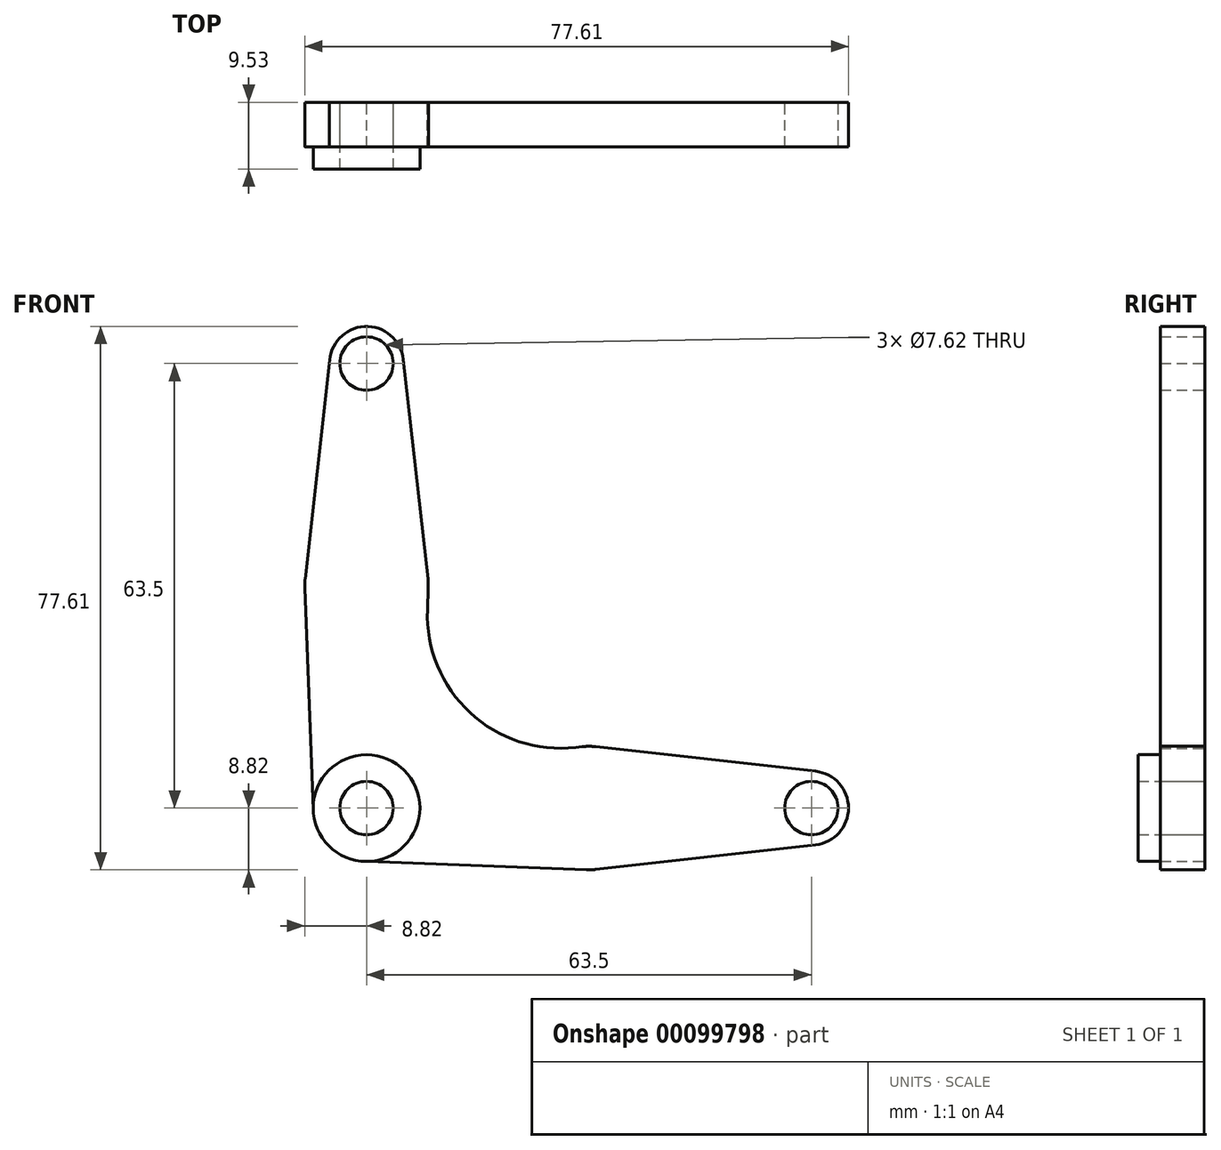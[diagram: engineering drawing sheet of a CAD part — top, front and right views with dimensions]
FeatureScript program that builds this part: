
annotation { "Feature Type Name" : "Feature", "Feature Type Description" : "" }
export const myFeature = defineFeature(function(context is Context, id is Id, definition is map)
    precondition{}
    {
        {
            var Q0;
            Q0=qCreatedBy(makeId("Front.planeOp"),FACE);
            var sketch = newSketch(context, id + "F0", { "sketchPlane" : qUnion([Q0])});
            skLineSegment(sketch, "E0", {"start": v(0, 0) * mm, "end": v(63.5, 0) * mm, "construction": true});
            skCircle(sketch, "E1", {"center": v(0, 63.5) * mm, "radius": 5.3 * mm});
            skCircle(sketch, "E2", {"center": v(0, 31.75) * mm, "radius": 8.82 * mm});
            skCircle(sketch, "E3", {"center": v(0, 0) * mm, "radius": 7.62 * mm});
            skCircle(sketch, "E4", {"center": v(63.5, 0) * mm, "radius": 5.3 * mm});
            skLineSegment(sketch, "E5", {"start": v(-5.3, 63.5) * mm, "end": v(-8.76, 32.74) * mm});
            skLineSegment(sketch, "E6", {"start": v(8.76, 32.73) * mm, "end": v(5.26, 64.09) * mm});
            skLineSegment(sketch, "E7", {"start": v(0, 63.5) * mm, "end": v(0, 0) * mm, "construction": true});
            skCircle(sketch, "E8", {"center": v(0, 63.5) * mm, "radius": 3.81 * mm});
            skCircle(sketch, "E9", {"center": v(0, 0) * mm, "radius": 3.81 * mm});
            skCircle(sketch, "E10", {"center": v(63.5, 0) * mm, "radius": 3.81 * mm});
            skLineSegment(sketch, "E11", {"start": v(-8.81, 31.42) * mm, "end": v(-7.61, -0.29) * mm});
            skLineSegment(sketch, "E12", {"start": v(8.81, 31.42) * mm, "end": v(8.7, 28.31) * mm});
            skCircle(sketch, "E13", {"center": v(31.75, 0) * mm, "radius": 8.82 * mm});
            skLineSegment(sketch, "E14", {"start": v(29.85, 8.66) * mm, "end": v(30.77, 8.76) * mm});
            skLineSegment(sketch, "E15", {"start": v(0, -7.62) * mm, "end": v(31.42, -8.81) * mm});
            skLineSegment(sketch, "E16", {"start": v(32.73, 8.76) * mm, "end": v(64.09, 5.26) * mm});
            skLineSegment(sketch, "E17", {"start": v(32.73, -8.76) * mm, "end": v(64.09, -5.26) * mm});
            skPoint(sketch, "E18.newPointB", {"position": v(0, 5.32) * mm});
            skArc(sketch, "E18.filletArc", {"start": v(8.7, 28.31) * mm, "mid": v(14.77, 13.64) * mm, "end": v(29.85, 8.66) * mm});
            skSolve(sketch);
        }
        {
            var Q0;
            Q0=makeQuery(id+"F0.imprint","IMPRINT",FACE,{"disambiguationData":[TD([[makeQuery(id+"F0.imprint","IMPRINT",EDGE,{"derivedFrom":sQuery(id+"F0.wireOp",EDGE,"yJPejFJz-5Hof-ibUk-N60A-88DD0Kfbzzva")}),1.0]])]});
            var Q1;
            Q1=makeQuery(id+"F0.imprint","IMPRINT",FACE,{"disambiguationData":[TD([[makeQuery(id+"F0.imprint","IMPRINT",EDGE,{"derivedFrom":sQuery(id+"F0.wireOp",EDGE,"yJPejFJz-5Hof-ibUk-N60A-88DD0Kfbzzva")}),-1.0]])]});
            var Q2;
            Q2=makeQuery(id+"F0.imprint","IMPRINT",FACE,{"disambiguationData":[TD([[makeQuery(id+"F0.imprint","IMPRINT",EDGE,{"derivedFrom":sQuery(id+"F0.wireOp",EDGE,"E10")}),-1.0]])]});
            var Q3;
            {var subQ0=sQuery(id+"F0.wireOp",EDGE,"E5");Q3=makeQuery(id+"F0.imprint","IMPRINT",FACE,{"disambiguationData":[TD([[makeQuery(id+"F0.imprint","IMPRINT",EDGE,{"derivedFrom":subQ0}),1.0]])]});}
            var Q4;
            Q4=makeQuery(id+"F0.imprint","IMPRINT",FACE,{"disambiguationData":[TD([[makeQuery(id+"F0.imprint","IMPRINT",EDGE,{"derivedFrom":sQuery(id+"F0.wireOp",EDGE,"E8")}),-1.0]])]});
            var Q5;
            {var subQ1=sQuery(id+"F0.wireOp",EDGE,"E11");Q5=makeQuery(id+"F0.imprint","IMPRINT",FACE,{"disambiguationData":[TD([[makeQuery(id+"F0.imprint","IMPRINT",EDGE,{"derivedFrom":subQ1}),1.0]])]});}
            var Q6;
            {var subQ0=sQuery(id+"F0.wireOp",EDGE,"E13");var subQ1=makeQuery(id+"F0.imprint","INTERSECT",VERTEX,{"derivedFrom":[subQ0,sQuery(id+"F0.wireOp",EDGE,"E14")]});Q6=makeQuery(id+"F0.imprint","IMPRINT",FACE,{"disambiguationData":[TD([[makeQuery(id+"F0.imprint","IMPRINT",EDGE,{"disambiguationData":[TD([[subQ1,1.0]])],"derivedFrom":subQ0}),1.0]])]});}
            var Q7;
            {var subQ0=sQuery(id+"F0.wireOp",EDGE,"E16");Q7=makeQuery(id+"F0.imprint","IMPRINT",FACE,{"disambiguationData":[TD([[makeQuery(id+"F0.imprint","IMPRINT",EDGE,{"derivedFrom":subQ0}),-1.0]])]});}
            var Q8;
            Q8=makeQuery(id+"F0.imprint","IMPRINT",FACE,{"disambiguationData":[TD([[makeQuery(id+"F0.imprint","IMPRINT",EDGE,{"derivedFrom":sQuery(id+"F0.wireOp",EDGE,"E9")}),-1.0]])]});
            var Q9;
            {var subQ0=sQuery(id+"F0.wireOp",EDGE,"E2");var subQ1=makeQuery(id+"F0.imprint","INTERSECT",VERTEX,{"derivedFrom":[subQ0,sQuery(id+"F0.wireOp",EDGE,"E5")]});Q9=makeQuery(id+"F0.imprint","IMPRINT",FACE,{"disambiguationData":[TD([[makeQuery(id+"F0.imprint","IMPRINT",EDGE,{"disambiguationData":[TD([[subQ1,1.0]])],"derivedFrom":subQ0}),1.0]])]});}
            extrude(context, id + "F1", {"entities" : qUnion([Q0, Q1, Q2, Q3, Q4, Q5, Q6, Q7, Q8, Q9]), "depth" : 6.35 * mm});
        }
        {
            var Q0;
            Q0=makeQuery(id+"F1.opExtrude","CAP_FACE",FACE,{"disambiguationData":[OSD([sQuery(id+"F0.wireOp",EDGE,"E1"),sQuery(id+"F0.wireOp",EDGE,"E2"),sQuery(id+"F0.wireOp",EDGE,"E3"),sQuery(id+"F0.wireOp",EDGE,"E4"),sQuery(id+"F0.wireOp",EDGE,"E5"),sQuery(id+"F0.wireOp",EDGE,"E6"),sQuery(id+"F0.wireOp",EDGE,"E8"),sQuery(id+"F0.wireOp",EDGE,"E9"),sQuery(id+"F0.wireOp",EDGE,"E10"),sQuery(id+"F0.wireOp",EDGE,"E11"),sQuery(id+"F0.wireOp",EDGE,"E12"),sQuery(id+"F0.wireOp",EDGE,"E13"),sQuery(id+"F0.wireOp",EDGE,"E14"),sQuery(id+"F0.wireOp",EDGE,"E15"),sQuery(id+"F0.wireOp",EDGE,"E16"),sQuery(id+"F0.wireOp",EDGE,"E17"),sQuery(id+"F0.wireOp",EDGE,"E18.filletArc")])],"isStart":false});
            var sketch = newSketch(context, id + "F2", { "sketchPlane" : qUnion([Q0])});
            skCircle(sketch, "E19", {"center": v(0, 0) * mm, "radius": 7.62 * mm});
            skCircle(sketch, "E20", {"center": v(0, 0) * mm, "radius": 3.81 * mm});
            skSolve(sketch);
        }
        {
            var Q0;
            Q0=makeQuery(id+"F2.imprint","IMPRINT",FACE,{"disambiguationData":[TD([[makeQuery(id+"F2.imprint","IMPRINT",EDGE,{"derivedFrom":sQuery(id+"F2.wireOp",EDGE,"E20")}),-1.0]])]});
            extrude(context, id + "F3", {"entities" : qUnion([Q0]), "operationType" : NewBodyOperationType.ADD, "depth" : 3.17 * mm});
        }
    });
